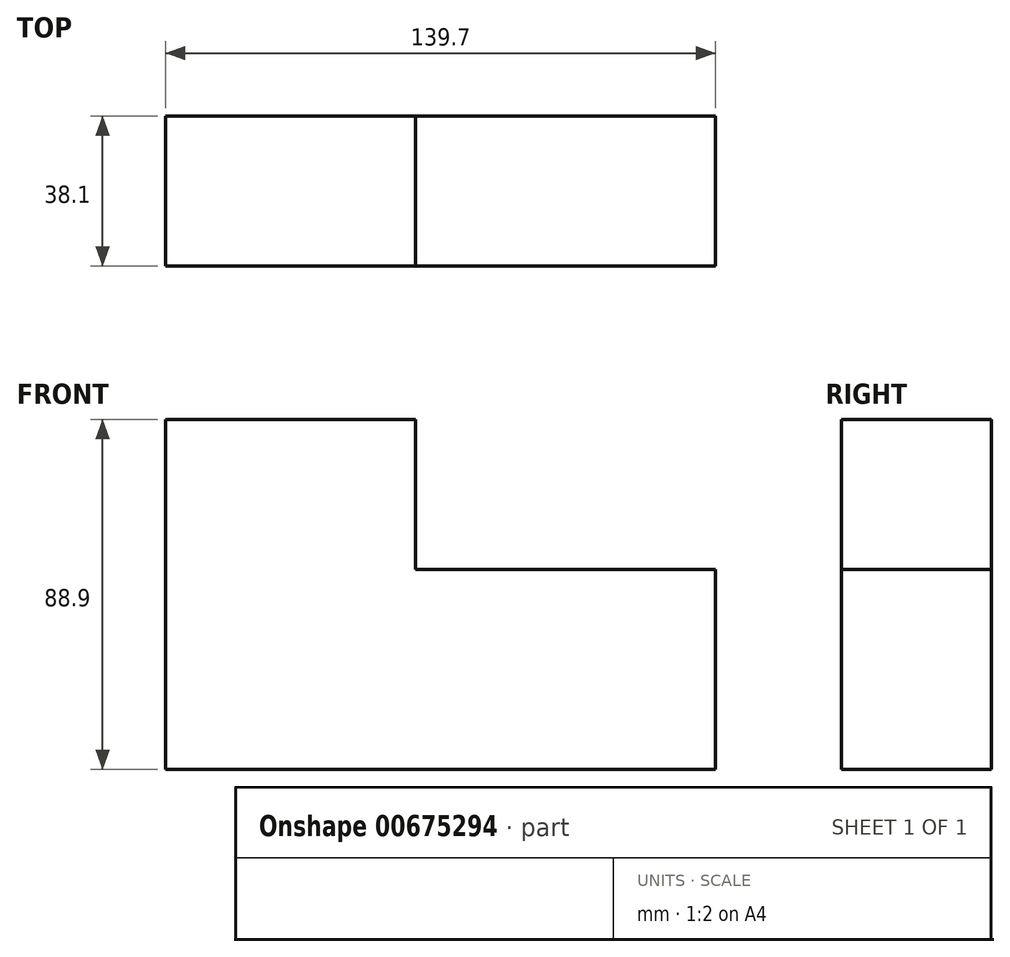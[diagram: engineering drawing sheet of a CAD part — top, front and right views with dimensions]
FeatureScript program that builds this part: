
annotation { "Feature Type Name" : "Feature", "Feature Type Description" : "" }
export const myFeature = defineFeature(function(context is Context, id is Id, definition is map)
    precondition{}
    {
        {
            var Q0;
            Q0=qCreatedBy(makeId("Front.planeOp"),FACE);
            var sketch = newSketch(context, id + "F0", { "sketchPlane" : qUnion([Q0])});
            skLineSegment(sketch, "E0", {"start": v(-63.5, -30.84) * mm, "end": v(76.2, -30.84) * mm});
            skLineSegment(sketch, "E1", {"start": v(76.2, 19.96) * mm, "end": v(76.2, -30.84) * mm});
            skLineSegment(sketch, "E2", {"start": v(76.2, 19.96) * mm, "end": v(0, 19.96) * mm});
            skLineSegment(sketch, "E3", {"start": v(0, 19.96) * mm, "end": v(0, 58.06) * mm});
            skLineSegment(sketch, "E4", {"start": v(-63.5, -30.84) * mm, "end": v(-63.5, 58.06) * mm});
            skLineSegment(sketch, "E5", {"start": v(0, 58.06) * mm, "end": v(-63.5, 58.06) * mm});
            skSolve(sketch);
        }
        {
            var Q0;
            Q0=makeQuery(id+"F0.imprint","IMPRINT",FACE,{"disambiguationData":[TD([[makeQuery(id+"F0.imprint","IMPRINT",EDGE,{"derivedFrom":sQuery(id+"F0.wireOp",EDGE,"E0")}),1.0]])]});
            extrude(context, id + "F1", {"entities" : qUnion([Q0]), "depth" : 38.1 * mm, "offsetDistance" : 25.4 * mm});
        }
    });
